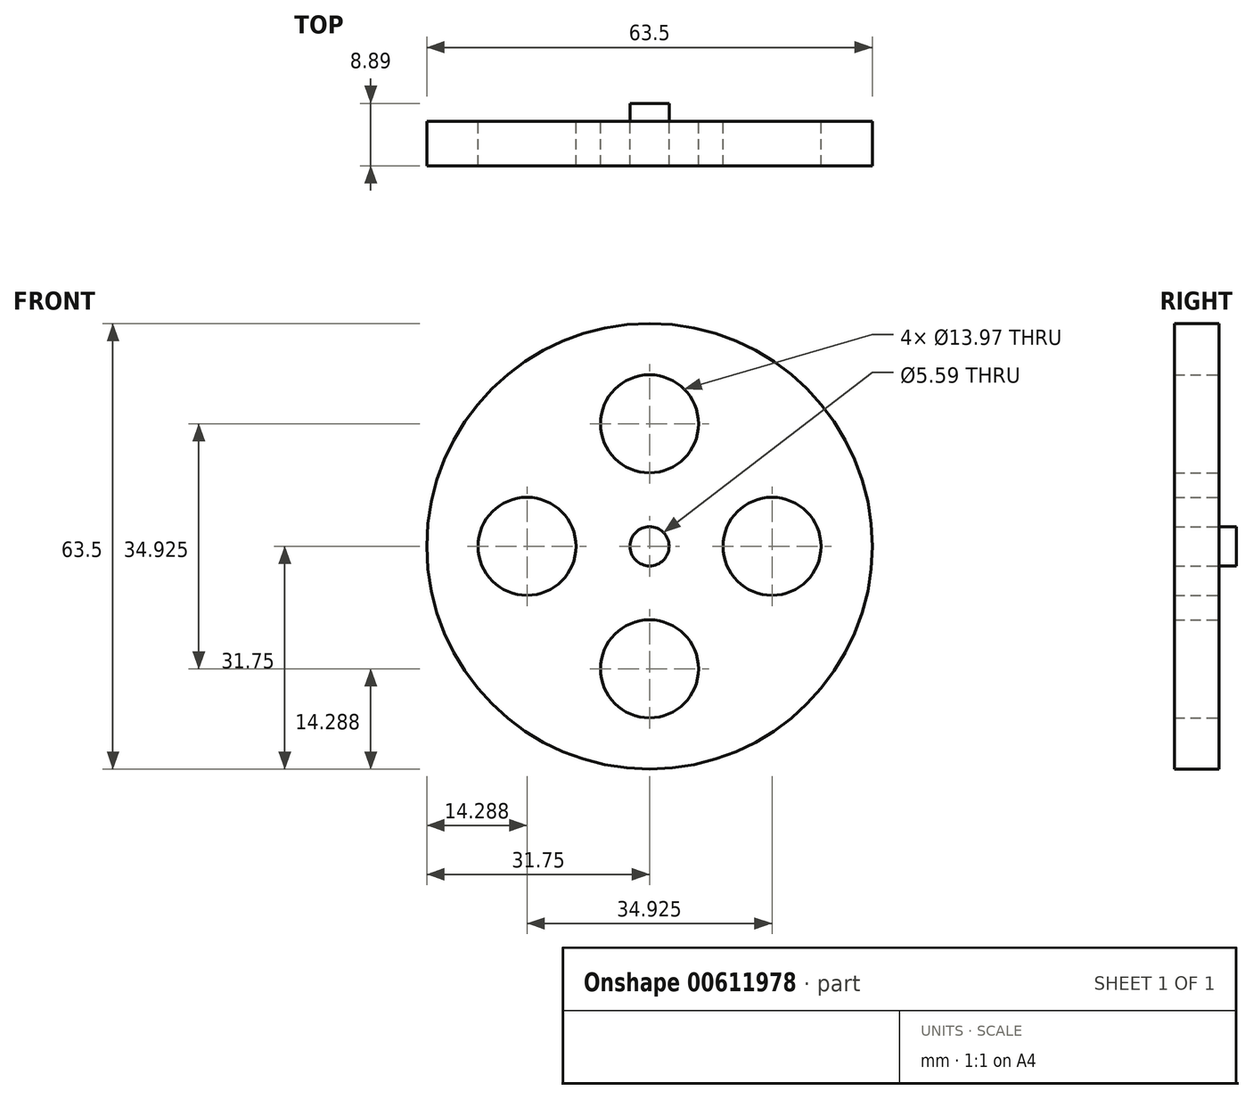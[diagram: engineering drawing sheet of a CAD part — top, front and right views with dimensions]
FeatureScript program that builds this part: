
annotation { "Feature Type Name" : "Feature", "Feature Type Description" : "" }
export const myFeature = defineFeature(function(context is Context, id is Id, definition is map)
    precondition{}
    {
        {
            var Q0;
            Q0=qCreatedBy(makeId("Front.planeOp"),FACE);
            var sketch = newSketch(context, id + "F0", { "sketchPlane" : qUnion([Q0])});
            skCircle(sketch, "E0", {"center": v(0, 0) * mm, "radius": 31.75 * mm});
            skCircle(sketch, "E1", {"center": v(0, 0) * mm, "radius": 2.8 * mm});
            skCircle(sketch, "E2", {"center": v(0, -17.46) * mm, "radius": 6.99 * mm});
            skCircle(sketch, "E3.1.0", {"center": v(17.46, 0) * mm, "radius": 6.99 * mm});
            skCircle(sketch, "E3.2.0", {"center": v(0, 17.46) * mm, "radius": 6.99 * mm});
            skCircle(sketch, "E3.3.0", {"center": v(-17.46, 0) * mm, "radius": 6.99 * mm});
            skSolve(sketch);
        }
        {
            var Q0;
            Q0=qSketchRegion(id+"F0",true);
            extrude(context, id + "F1", {"entities" : qUnion([Q0]), "depth" : 6.35 * mm, "offsetDistance" : 25.4 * mm});
        }
        {
            var Q0;
            Q0=makeQuery(id+"F0.imprint","IMPRINT",FACE,{"disambiguationData":[TD([[makeQuery(id+"F0.imprint","IMPRINT",EDGE,{"derivedFrom":sQuery(id+"F0.wireOp",EDGE,"E1")}),1.0]])]});
            extrude(context, id + "F2", {"entities" : qUnion([Q0]), "oppositeDirection" : true, "depth" : 2.54 * mm, "offsetDistance" : 25.4 * mm});
        }
    });
